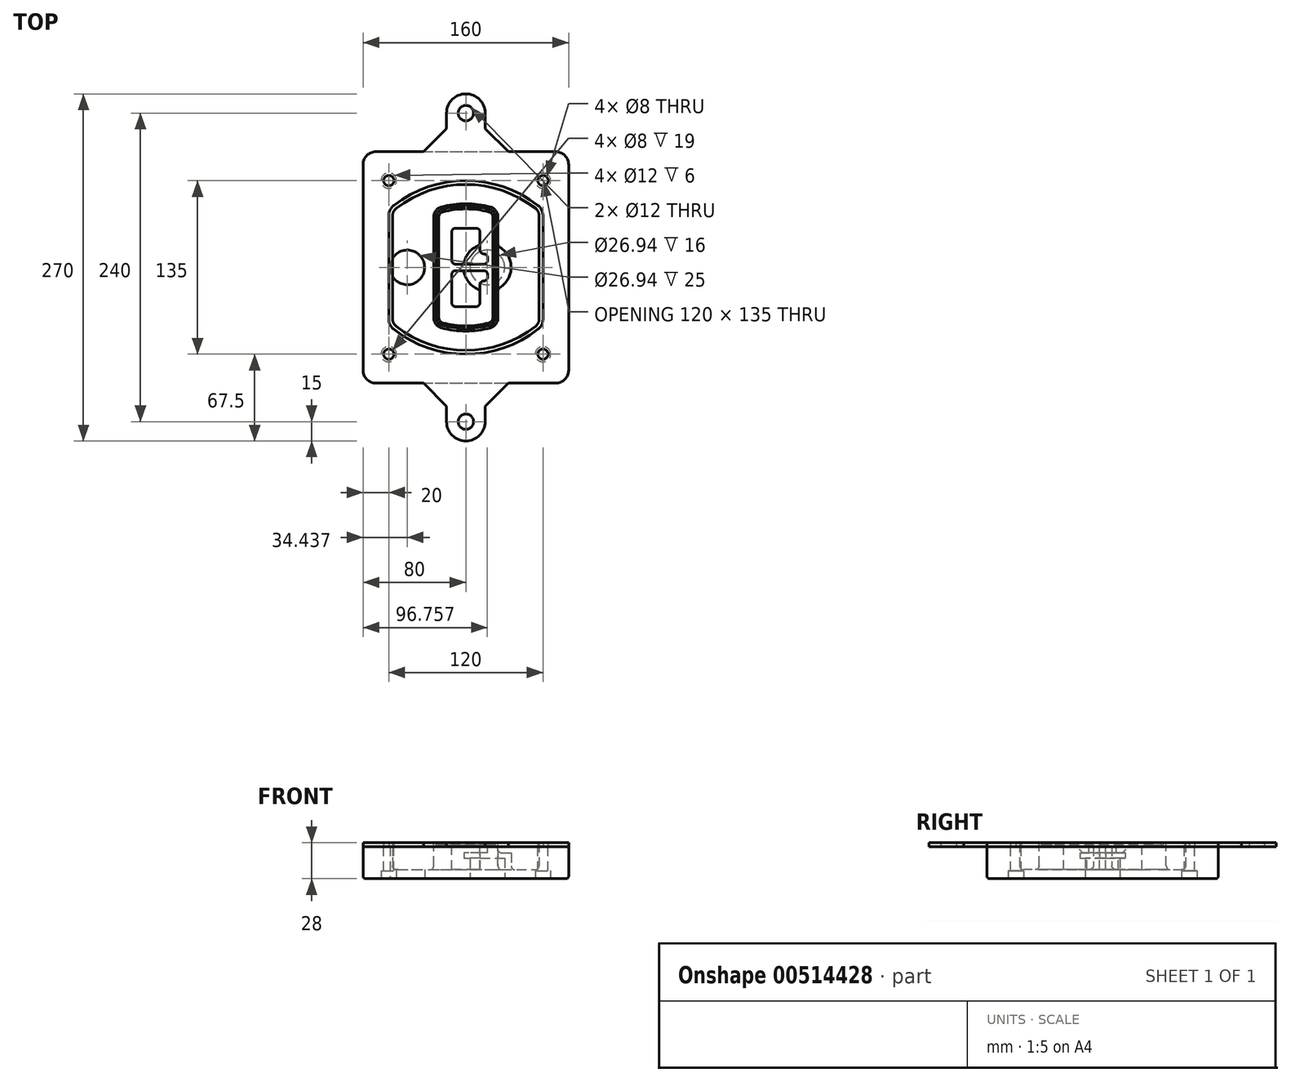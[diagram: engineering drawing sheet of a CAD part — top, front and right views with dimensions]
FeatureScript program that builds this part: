
annotation { "Feature Type Name" : "Feature", "Feature Type Description" : "" }
export const myFeature = defineFeature(function(context is Context, id is Id, definition is map)
    precondition{}
    {
        {
            var Q0;
            Q0=qCreatedBy(makeId("Top.planeOp"),FACE);
            var sketch = newSketch(context, id + "F0", { "sketchPlane" : qUnion([Q0])});
            skPoint(sketch, "E0.rect.middle", {"position": v(0, 0) * mm});
            skLineSegment(sketch, "E1.bottom", {"start": v(-70, -90) * mm, "end": v(70, -90) * mm});
            skLineSegment(sketch, "E1.top", {"start": v(-70, 90) * mm, "end": v(70, 90) * mm});
            skLineSegment(sketch, "E1.left", {"start": v(-80, -80) * mm, "end": v(-80, 80) * mm});
            skLineSegment(sketch, "E1.right", {"start": v(80, -80) * mm, "end": v(80, 80) * mm});
            skLineSegment(sketch, "E2", {"start": v(-80, 90) * mm, "end": v(80, -90) * mm, "construction": true});
            skLineSegment(sketch, "E3", {"start": v(80, 90) * mm, "end": v(-80, -90) * mm, "construction": true});
            skCircle(sketch, "E4", {"center": v(-60, 67.5) * mm, "radius": 4 * mm});
            skCircle(sketch, "E5", {"center": v(60, 67.5) * mm, "radius": 4 * mm});
            skCircle(sketch, "E6", {"center": v(60, -67.5) * mm, "radius": 4 * mm});
            skCircle(sketch, "E7", {"center": v(-60, -67.5) * mm, "radius": 4 * mm});
            skLineSegment(sketch, "E8", {"start": v(-60, 67.5) * mm, "end": v(60, 67.5) * mm, "construction": true});
            skLineSegment(sketch, "E9", {"start": v(60, 67.5) * mm, "end": v(60, -67.5) * mm, "construction": true});
            skLineSegment(sketch, "E10", {"start": v(60, -67.5) * mm, "end": v(-60, -67.5) * mm, "construction": true});
            skLineSegment(sketch, "E11", {"start": v(-60, -67.5) * mm, "end": v(-60, 67.5) * mm, "construction": true});
            skLineSegment(sketch, "E12", {"start": v(-60, 40.3) * mm, "end": v(-60, -40.3) * mm});
            skLineSegment(sketch, "E13", {"start": v(60, 40.3) * mm, "end": v(60, -40.3) * mm});
            skArc(sketch, "E14", {"start": v(56.15, 48.18) * mm, "mid": v(0, 67.5) * mm, "end": v(-56.15, 48.18) * mm});
            skArc(sketch, "E15", {"start": v(-56.15, -48.18) * mm, "mid": v(0, -67.5) * mm, "end": v(56.15, -48.18) * mm});
            skLineSegment(sketch, "E16", {"start": v(-60, 0) * mm, "end": v(60, 0) * mm, "construction": true});
            skPoint(sketch, "E17.visualSharp", {"position": v(-60, -45) * mm});
            skArc(sketch, "E17.filletArc", {"start": v(-60, -40.3) * mm, "mid": v(-58.99, -44.68) * mm, "end": v(-56.15, -48.18) * mm});
            skPoint(sketch, "E18.visualSharp", {"position": v(-60, 45) * mm});
            skArc(sketch, "E18.filletArc", {"start": v(-56.15, 48.18) * mm, "mid": v(-58.99, 44.68) * mm, "end": v(-60, 40.3) * mm});
            skPoint(sketch, "E19.visualSharp", {"position": v(60, 45) * mm});
            skArc(sketch, "E19.filletArc", {"start": v(60, 40.3) * mm, "mid": v(58.99, 44.68) * mm, "end": v(56.15, 48.18) * mm});
            skPoint(sketch, "E20.visualSharp", {"position": v(60, -45) * mm});
            skArc(sketch, "E20.filletArc", {"start": v(56.15, -48.18) * mm, "mid": v(58.99, -44.68) * mm, "end": v(60, -40.3) * mm});
            skPoint(sketch, "E21.visualSharp", {"position": v(-80, 90) * mm});
            skArc(sketch, "E21.filletArc", {"start": v(-70, 90) * mm, "mid": v(-77.07, 87.07) * mm, "end": v(-80, 80) * mm});
            skPoint(sketch, "E22.visualSharp", {"position": v(80, 90) * mm});
            skArc(sketch, "E22.filletArc", {"start": v(80, 80) * mm, "mid": v(77.07, 87.07) * mm, "end": v(70, 90) * mm});
            skPoint(sketch, "E23.visualSharp", {"position": v(80, -90) * mm});
            skArc(sketch, "E23.filletArc", {"start": v(70, -90) * mm, "mid": v(77.07, -87.07) * mm, "end": v(80, -80) * mm});
            skPoint(sketch, "E24.visualSharp", {"position": v(-80, -90) * mm});
            skArc(sketch, "E24.filletArc", {"start": v(-80, -80) * mm, "mid": v(-77.07, -87.07) * mm, "end": v(-70, -90) * mm});
            skArc(sketch, "E25.0", {"start": v(57, 40.3) * mm, "mid": v(56.3, 43.36) * mm, "end": v(54.3, 45.81) * mm});
            skLineSegment(sketch, "E25.1", {"start": v(57, 40.3) * mm, "end": v(57, -40.3) * mm});
            skArc(sketch, "E25.2", {"start": v(54.3, -45.81) * mm, "mid": v(56.3, -43.36) * mm, "end": v(57, -40.3) * mm});
            skArc(sketch, "E25.3", {"start": v(-54.3, -45.81) * mm, "mid": v(0, -64.5) * mm, "end": v(54.3, -45.81) * mm});
            skArc(sketch, "E25.4", {"start": v(-57, -40.3) * mm, "mid": v(-56.3, -43.36) * mm, "end": v(-54.3, -45.81) * mm});
            skArc(sketch, "E25.5", {"start": v(54.3, 45.81) * mm, "mid": v(0, 64.5) * mm, "end": v(-54.3, 45.81) * mm});
            skLineSegment(sketch, "E25.6", {"start": v(-57, 40.3) * mm, "end": v(-57, -40.3) * mm});
            skArc(sketch, "E25.7", {"start": v(-54.3, 45.81) * mm, "mid": v(-56.3, 43.36) * mm, "end": v(-57, 40.3) * mm});
            skArc(sketch, "E26.0", {"start": v(-58.62, 51.33) * mm, "mid": v(-62.58, 46.43) * mm, "end": v(-64, 40.3) * mm});
            skArc(sketch, "E26.1", {"start": v(58.62, 51.33) * mm, "mid": v(0, 71.5) * mm, "end": v(-58.62, 51.33) * mm});
            skArc(sketch, "E26.2", {"start": v(64, 40.3) * mm, "mid": v(62.58, 46.43) * mm, "end": v(58.62, 51.33) * mm});
            skLineSegment(sketch, "E26.3", {"start": v(64, 40.3) * mm, "end": v(64, -40.3) * mm});
            skArc(sketch, "E26.4", {"start": v(58.62, -51.33) * mm, "mid": v(62.58, -46.43) * mm, "end": v(64, -40.3) * mm});
            skLineSegment(sketch, "E26.5", {"start": v(-64, 40.3) * mm, "end": v(-64, -40.3) * mm});
            skArc(sketch, "E26.6", {"start": v(-58.62, -51.33) * mm, "mid": v(0, -71.5) * mm, "end": v(58.62, -51.33) * mm});
            skArc(sketch, "E26.7", {"start": v(-64, -40.3) * mm, "mid": v(-62.58, -46.43) * mm, "end": v(-58.62, -51.33) * mm});
            skSolve(sketch);
        }
        {
            var Q0;
            Q0=makeQuery(id+"F0.imprint","IMPRINT",FACE,{"disambiguationData":[TD([[makeQuery(id+"F0.imprint","IMPRINT",EDGE,{"derivedFrom":sQuery(id+"F0.wireOp",EDGE,"E1.bottom")}),1.0]])]});
            var Q1;
            Q1=makeQuery(id+"F0.imprint","IMPRINT",FACE,{"disambiguationData":[TD([[makeQuery(id+"F0.imprint","IMPRINT",EDGE,{"derivedFrom":sQuery(id+"F0.wireOp",EDGE,"E12")}),1.0]])]});
            var Q2;
            Q2=makeQuery(id+"F0.imprint","IMPRINT",FACE,{"disambiguationData":[TD([[makeQuery(id+"F0.imprint","IMPRINT",EDGE,{"derivedFrom":sQuery(id+"F0.wireOp",EDGE,"E25.0")}),1.0]])]});
            var Q3;
            Q3=makeQuery(id+"F0.imprint","IMPRINT",FACE,{"disambiguationData":[TD([[makeQuery(id+"F0.imprint","IMPRINT",EDGE,{"derivedFrom":sQuery(id+"F0.wireOp",EDGE,"E12")}),-1.0]])]});
            extrude(context, id + "F1", {"entities" : qUnion([Q0, Q1, Q2, Q3]), "oppositeDirection" : true, "depth" : 25 * mm});
        }
        {
            var Q0;
            Q0=makeQuery(id+"F0.imprint","IMPRINT",FACE,{"disambiguationData":[TD([[makeQuery(id+"F0.imprint","IMPRINT",EDGE,{"derivedFrom":sQuery(id+"F0.wireOp",EDGE,"E12")}),1.0]])]});
            extrude(context, id + "F2", {"entities" : qUnion([Q0]), "operationType" : NewBodyOperationType.ADD, "depth" : 3 * mm, "offsetDistance" : 25 * mm});
        }
        {
            var Q0;
            Q0=makeQuery(id+"F0.imprint","IMPRINT",FACE,{"disambiguationData":[TD([[makeQuery(id+"F0.imprint","IMPRINT",EDGE,{"derivedFrom":sQuery(id+"F0.wireOp",EDGE,"E25.0")}),1.0]])]});
            extrude(context, id + "F3", {"entities" : qUnion([Q0]), "operationType" : NewBodyOperationType.REMOVE, "oppositeDirection" : true, "depth" : 18 * mm});
        }
        {
            var Q0;
            Q0=makeQuery(id+"F2.opExtrude","CAP_FACE",FACE,{"disambiguationData":[OSD([sQuery(id+"F0.wireOp",EDGE,"E12"),sQuery(id+"F0.wireOp",EDGE,"E13"),sQuery(id+"F0.wireOp",EDGE,"E14"),sQuery(id+"F0.wireOp",EDGE,"E15"),sQuery(id+"F0.wireOp",EDGE,"E17.filletArc"),sQuery(id+"F0.wireOp",EDGE,"E18.filletArc"),sQuery(id+"F0.wireOp",EDGE,"E19.filletArc"),sQuery(id+"F0.wireOp",EDGE,"E20.filletArc"),sQuery(id+"F0.wireOp",EDGE,"E25.0"),sQuery(id+"F0.wireOp",EDGE,"E25.1"),sQuery(id+"F0.wireOp",EDGE,"E25.2"),sQuery(id+"F0.wireOp",EDGE,"E25.3"),sQuery(id+"F0.wireOp",EDGE,"E25.4"),sQuery(id+"F0.wireOp",EDGE,"E25.5"),sQuery(id+"F0.wireOp",EDGE,"E25.6"),sQuery(id+"F0.wireOp",EDGE,"E25.7")])],"isStart":false});
            var sketch = newSketch(context, id + "F4", { "sketchPlane" : qUnion([Q0])});
            skArc(sketch, "E27.0", {"start": v(-19.08, -46.97) * mm, "mid": v(0, -49.5) * mm, "end": v(19.08, -46.97) * mm});
            skArc(sketch, "E28.0", {"start": v(19.08, 46.97) * mm, "mid": v(0, 49.5) * mm, "end": v(-19.08, 46.97) * mm});
            skLineSegment(sketch, "E29", {"start": v(-25, 39.25) * mm, "end": v(-25, -39.25) * mm});
            skLineSegment(sketch, "E30", {"start": v(25, 39.25) * mm, "end": v(25, -39.25) * mm});
            skLineSegment(sketch, "E31", {"start": v(-25, 45.1) * mm, "end": v(25, 45.1) * mm, "construction": true});
            skLineSegment(sketch, "E32", {"start": v(-25, -45.1) * mm, "end": v(25, -45.1) * mm, "construction": true});
            skPoint(sketch, "E33.visualSharp", {"position": v(-25, 45.1) * mm});
            skArc(sketch, "E33.filletArc", {"start": v(-19.08, 46.97) * mm, "mid": v(-23.35, 44.11) * mm, "end": v(-25, 39.25) * mm});
            skPoint(sketch, "E34.visualSharp", {"position": v(25, 45.1) * mm});
            skArc(sketch, "E34.filletArc", {"start": v(25, 39.25) * mm, "mid": v(23.35, 44.11) * mm, "end": v(19.08, 46.97) * mm});
            skPoint(sketch, "E35.visualSharp", {"position": v(25, -45.1) * mm});
            skArc(sketch, "E35.filletArc", {"start": v(19.08, -46.97) * mm, "mid": v(23.35, -44.11) * mm, "end": v(25, -39.25) * mm});
            skPoint(sketch, "E36.visualSharp", {"position": v(-25, -45.1) * mm});
            skArc(sketch, "E36.filletArc", {"start": v(-25, -39.25) * mm, "mid": v(-23.35, -44.11) * mm, "end": v(-19.08, -46.97) * mm});
            skArc(sketch, "E37.0", {"start": v(54.3, 45.81) * mm, "mid": v(0, 64.5) * mm, "end": v(-54.3, 45.81) * mm});
            skArc(sketch, "E37.1", {"start": v(-54.3, 45.81) * mm, "mid": v(-56.3, 43.36) * mm, "end": v(-57, 40.3) * mm});
            skLineSegment(sketch, "E37.2", {"start": v(-57, 40.3) * mm, "end": v(-57, -40.3) * mm});
            skArc(sketch, "E37.3", {"start": v(-57, -40.3) * mm, "mid": v(-56.3, -43.36) * mm, "end": v(-54.3, -45.81) * mm});
            skArc(sketch, "E37.4", {"start": v(-54.3, -45.81) * mm, "mid": v(0, -64.5) * mm, "end": v(54.3, -45.81) * mm});
            skArc(sketch, "E37.5", {"start": v(54.3, -45.81) * mm, "mid": v(56.3, -43.36) * mm, "end": v(57, -40.3) * mm});
            skLineSegment(sketch, "E37.6", {"start": v(57, 40.3) * mm, "end": v(57, -40.3) * mm});
            skArc(sketch, "E37.7", {"start": v(57, 40.3) * mm, "mid": v(56.3, 43.36) * mm, "end": v(54.3, 45.81) * mm});
            skLineSegment(sketch, "E38.0", {"start": v(23, 39.25) * mm, "end": v(23, -39.25) * mm});
            skArc(sketch, "E38.1", {"start": v(18.56, -45.04) * mm, "mid": v(21.76, -42.9) * mm, "end": v(23, -39.25) * mm});
            skArc(sketch, "E38.2", {"start": v(-18.56, -45.04) * mm, "mid": v(0, -47.5) * mm, "end": v(18.56, -45.04) * mm});
            skArc(sketch, "E38.3", {"start": v(-23, -39.25) * mm, "mid": v(-21.76, -42.9) * mm, "end": v(-18.56, -45.04) * mm});
            skLineSegment(sketch, "E38.4", {"start": v(-23, 39.25) * mm, "end": v(-23, -39.25) * mm});
            skArc(sketch, "E38.5", {"start": v(23, 39.25) * mm, "mid": v(21.76, 42.9) * mm, "end": v(18.56, 45.04) * mm});
            skArc(sketch, "E38.6", {"start": v(-18.56, 45.04) * mm, "mid": v(-21.76, 42.9) * mm, "end": v(-23, 39.25) * mm});
            skArc(sketch, "E38.7", {"start": v(18.56, 45.04) * mm, "mid": v(0, 47.5) * mm, "end": v(-18.56, 45.04) * mm});
            skArc(sketch, "E39.0", {"start": v(21, 39.25) * mm, "mid": v(20.18, 41.68) * mm, "end": v(18.04, 43.1) * mm});
            skLineSegment(sketch, "E39.1", {"start": v(21, 39.25) * mm, "end": v(21, -39.25) * mm});
            skArc(sketch, "E39.2", {"start": v(18.04, -43.1) * mm, "mid": v(20.18, -41.68) * mm, "end": v(21, -39.25) * mm});
            skArc(sketch, "E39.3", {"start": v(-18.04, -43.1) * mm, "mid": v(0, -45.5) * mm, "end": v(18.04, -43.1) * mm});
            skArc(sketch, "E39.4", {"start": v(-21, -39.25) * mm, "mid": v(-20.18, -41.68) * mm, "end": v(-18.04, -43.1) * mm});
            skArc(sketch, "E39.5", {"start": v(18.04, 43.1) * mm, "mid": v(0, 45.5) * mm, "end": v(-18.04, 43.1) * mm});
            skLineSegment(sketch, "E39.6", {"start": v(-21, 39.25) * mm, "end": v(-21, -39.25) * mm});
            skArc(sketch, "E39.7", {"start": v(-18.04, 43.1) * mm, "mid": v(-20.18, 41.68) * mm, "end": v(-21, 39.25) * mm});
            skLineSegment(sketch, "E40", {"start": v(-25, 0) * mm, "end": v(25, 0) * mm, "construction": true});
            skLineSegment(sketch, "E41", {"start": v(-11, 5.5) * mm, "end": v(-11, 27.5) * mm});
            skLineSegment(sketch, "E42", {"start": v(-8, 30.5) * mm, "end": v(8, 30.5) * mm});
            skLineSegment(sketch, "E43", {"start": v(11, 27.5) * mm, "end": v(11, 13.5) * mm});
            skLineSegment(sketch, "E44", {"start": v(14, 10.5) * mm, "end": v(14, 10.5) * mm});
            skLineSegment(sketch, "E45", {"start": v(17, 7.5) * mm, "end": v(17, 5.5) * mm});
            skLineSegment(sketch, "E46", {"start": v(14, 2.5) * mm, "end": v(-8, 2.5) * mm});
            skPoint(sketch, "E47.visualSharp", {"position": v(-11, 30.5) * mm});
            skArc(sketch, "E47.filletArc", {"start": v(-8, 30.5) * mm, "mid": v(-10.12, 29.62) * mm, "end": v(-11, 27.5) * mm});
            skPoint(sketch, "E48.visualSharp", {"position": v(11, 30.5) * mm});
            skArc(sketch, "E48.filletArc", {"start": v(11, 27.5) * mm, "mid": v(10.12, 29.62) * mm, "end": v(8, 30.5) * mm});
            skPoint(sketch, "E49.visualSharp", {"position": v(11, 10.5) * mm});
            skArc(sketch, "E49.filletArc", {"start": v(11, 13.5) * mm, "mid": v(11.88, 11.38) * mm, "end": v(14, 10.5) * mm});
            skPoint(sketch, "E50.visualSharp", {"position": v(17, 10.5) * mm});
            skArc(sketch, "E50.filletArc", {"start": v(17, 7.5) * mm, "mid": v(16.12, 9.62) * mm, "end": v(14, 10.5) * mm});
            skPoint(sketch, "E51.visualSharp", {"position": v(17, 2.5) * mm});
            skArc(sketch, "E51.filletArc", {"start": v(14, 2.5) * mm, "mid": v(16.12, 3.38) * mm, "end": v(17, 5.5) * mm});
            skPoint(sketch, "E52.visualSharp", {"position": v(-11, 2.5) * mm});
            skArc(sketch, "E52.filletArc", {"start": v(-11, 5.5) * mm, "mid": v(-10.12, 3.38) * mm, "end": v(-8, 2.5) * mm});
            skLineSegment(sketch, "E53.0.MirrorCS", {"start": v(14, -2.5) * mm, "end": v(-8, -2.5) * mm});
            skArc(sketch, "E54.0.MirrorCS", {"start": v(-11, -5.5) * mm, "mid": v(-10.12, -3.38) * mm, "end": v(-8, -2.5) * mm});
            skLineSegment(sketch, "E55.0.MirrorCS", {"start": v(-11, -5.5) * mm, "end": v(-11, -27.5) * mm});
            skArc(sketch, "E56.0.MirrorCS", {"start": v(-8, -30.5) * mm, "mid": v(-10.12, -29.62) * mm, "end": v(-11, -27.5) * mm});
            skLineSegment(sketch, "E57.0.MirrorCS", {"start": v(-8, -30.5) * mm, "end": v(8, -30.5) * mm});
            skArc(sketch, "E58.0.MirrorCS", {"start": v(11, -27.5) * mm, "mid": v(10.12, -29.62) * mm, "end": v(8, -30.5) * mm});
            skLineSegment(sketch, "E59.0.MirrorCS", {"start": v(11, -27.5) * mm, "end": v(11, -13.5) * mm});
            skArc(sketch, "E60.0.MirrorCS", {"start": v(11, -13.5) * mm, "mid": v(11.88, -11.38) * mm, "end": v(14, -10.5) * mm});
            skArc(sketch, "E61.0.MirrorCS", {"start": v(17, -7.5) * mm, "mid": v(16.12, -9.62) * mm, "end": v(14, -10.5) * mm});
            skLineSegment(sketch, "E62.0.MirrorCS", {"start": v(17, -7.5) * mm, "end": v(17, -5.5) * mm});
            skArc(sketch, "E63.0.MirrorCS", {"start": v(14, -2.5) * mm, "mid": v(16.12, -3.38) * mm, "end": v(17, -5.5) * mm});
            skSolve(sketch);
        }
        {
            var Q0;
            Q0=makeQuery(id+"F4.imprint","IMPRINT",FACE,{"disambiguationData":[TD([[makeQuery(id+"F4.imprint","IMPRINT",EDGE,{"derivedFrom":sQuery(id+"F4.wireOp",EDGE,"E27.0")}),1.0]])]});
            var Q1;
            Q1=makeQuery(id+"F4.imprint","IMPRINT",FACE,{"disambiguationData":[TD([[makeQuery(id+"F4.imprint","IMPRINT",EDGE,{"derivedFrom":sQuery(id+"F4.wireOp",EDGE,"E38.0")}),-1.0]])]});
            var Q2;
            Q2=makeQuery(id+"F4.imprint","IMPRINT",FACE,{"disambiguationData":[TD([[makeQuery(id+"F4.imprint","IMPRINT",EDGE,{"derivedFrom":sQuery(id+"F4.wireOp",EDGE,"E39.0")}),1.0]])]});
            extrude(context, id + "F5", {"entities" : qUnion([Q0, Q1, Q2]), "operationType" : NewBodyOperationType.ADD, "endBound" : BoundingType.UP_TO_NEXT, "oppositeDirection" : true, "depth" : 25 * mm});
        }
        {
            var Q0;
            Q0=makeQuery(id+"F4.imprint","IMPRINT",FACE,{"disambiguationData":[TD([[makeQuery(id+"F4.imprint","IMPRINT",EDGE,{"derivedFrom":sQuery(id+"F4.wireOp",EDGE,"E38.0")}),-1.0]])]});
            extrude(context, id + "F6", {"entities" : qUnion([Q0]), "operationType" : NewBodyOperationType.REMOVE, "oppositeDirection" : true, "depth" : 2 * mm});
        }
        {
            var Q0;
            Q0=makeQuery(id+"F1.opExtrude","CAP_FACE",FACE,{"disambiguationData":[OSD([sQuery(id+"F0.wireOp",EDGE,"E1.bottom"),sQuery(id+"F0.wireOp",EDGE,"E1.top"),sQuery(id+"F0.wireOp",EDGE,"E1.left"),sQuery(id+"F0.wireOp",EDGE,"E1.right"),sQuery(id+"F0.wireOp",EDGE,"E4"),sQuery(id+"F0.wireOp",EDGE,"E5"),sQuery(id+"F0.wireOp",EDGE,"E6"),sQuery(id+"F0.wireOp",EDGE,"E7"),sQuery(id+"F0.wireOp",EDGE,"E21.filletArc"),sQuery(id+"F0.wireOp",EDGE,"E22.filletArc"),sQuery(id+"F0.wireOp",EDGE,"E23.filletArc"),sQuery(id+"F0.wireOp",EDGE,"E24.filletArc")])],"isStart":false});
            var sketch = newSketch(context, id + "F7", { "sketchPlane" : qUnion([Q0])});
            skCircle(sketch, "E64", {"center": v(16.76, 0) * mm, "radius": 13.47 * mm});
            skCircle(sketch, "E65", {"center": v(-45.56, 0) * mm, "radius": 13.47 * mm});
            skLineSegment(sketch, "E66", {"start": v(80, 0) * mm, "end": v(-80, 0) * mm});
            skCircle(sketch, "E67", {"center": v(16.76, 0) * mm, "radius": 18.47 * mm});
            skCircle(sketch, "E68", {"center": v(60, -67.5) * mm, "radius": 6 * mm});
            skCircle(sketch, "E69", {"center": v(-60, -67.5) * mm, "radius": 6 * mm});
            skCircle(sketch, "E70", {"center": v(-60, 67.5) * mm, "radius": 6 * mm});
            skCircle(sketch, "E71", {"center": v(60, 67.5) * mm, "radius": 6 * mm});
            skSolve(sketch);
        }
        {
            var Q0;
            {var subQ1=sQuery(id+"F7.wireOp",EDGE,"E66");var subQ4=sQuery(id+"F7.wireOp",EDGE,"E64");var subQ6=makeQuery(id+"F7.imprint","INTERSECT",VERTEX,{"disambiguationData":[OD(0.0)],"derivedFrom":[subQ4,subQ1]});Q0=makeQuery(id+"F7.imprint","IMPRINT",FACE,{"disambiguationData":[TD([[makeQuery(id+"F7.imprint","IMPRINT",EDGE,{"disambiguationData":[TD([[subQ6,-1.0]])],"derivedFrom":subQ4}),-1.0]])]});}
            var Q1;
            {var subQ0=sQuery(id+"F7.wireOp",EDGE,"E66");var subQ1=sQuery(id+"F7.wireOp",EDGE,"E64");var subQ3=makeQuery(id+"F7.imprint","INTERSECT",VERTEX,{"disambiguationData":[OD(0.0)],"derivedFrom":[subQ1,subQ0]});Q1=makeQuery(id+"F7.imprint","IMPRINT",FACE,{"disambiguationData":[TD([[makeQuery(id+"F7.imprint","IMPRINT",EDGE,{"disambiguationData":[TD([[subQ3,-1.0]])],"derivedFrom":subQ1}),1.0]])]});}
            var Q2;
            {var subQ0=sQuery(id+"F7.wireOp",EDGE,"E66");var subQ1=sQuery(id+"F7.wireOp",EDGE,"E64");var subQ3=makeQuery(id+"F7.imprint","INTERSECT",VERTEX,{"disambiguationData":[OD(0.0)],"derivedFrom":[subQ1,subQ0]});Q2=makeQuery(id+"F7.imprint","IMPRINT",FACE,{"disambiguationData":[TD([[makeQuery(id+"F7.imprint","IMPRINT",EDGE,{"disambiguationData":[TD([[subQ3,1.0]])],"derivedFrom":subQ1}),1.0]])]});}
            var Q3;
            {var subQ1=sQuery(id+"F7.wireOp",EDGE,"E66");var subQ4=sQuery(id+"F7.wireOp",EDGE,"E64");var subQ6=makeQuery(id+"F7.imprint","INTERSECT",VERTEX,{"disambiguationData":[OD(0.0)],"derivedFrom":[subQ4,subQ1]});Q3=makeQuery(id+"F7.imprint","IMPRINT",FACE,{"disambiguationData":[TD([[makeQuery(id+"F7.imprint","IMPRINT",EDGE,{"disambiguationData":[TD([[subQ6,1.0]])],"derivedFrom":subQ4}),-1.0]])]});}
            extrude(context, id + "F8", {"entities" : qUnion([Q0, Q1, Q2, Q3]), "operationType" : NewBodyOperationType.ADD, "oppositeDirection" : true, "depth" : 20 * mm});
        }
        {
            var Q0;
            {var subQ0=sQuery(id+"F7.wireOp",EDGE,"E66");var subQ1=sQuery(id+"F7.wireOp",EDGE,"E64");var subQ3=makeQuery(id+"F7.imprint","INTERSECT",VERTEX,{"disambiguationData":[OD(0.0)],"derivedFrom":[subQ1,subQ0]});Q0=makeQuery(id+"F7.imprint","IMPRINT",FACE,{"disambiguationData":[TD([[makeQuery(id+"F7.imprint","IMPRINT",EDGE,{"disambiguationData":[TD([[subQ3,-1.0]])],"derivedFrom":subQ1}),1.0]])]});}
            var Q1;
            {var subQ0=sQuery(id+"F7.wireOp",EDGE,"E66");var subQ1=sQuery(id+"F7.wireOp",EDGE,"E64");var subQ3=makeQuery(id+"F7.imprint","INTERSECT",VERTEX,{"disambiguationData":[OD(0.0)],"derivedFrom":[subQ1,subQ0]});Q1=makeQuery(id+"F7.imprint","IMPRINT",FACE,{"disambiguationData":[TD([[makeQuery(id+"F7.imprint","IMPRINT",EDGE,{"disambiguationData":[TD([[subQ3,1.0]])],"derivedFrom":subQ1}),1.0]])]});}
            extrude(context, id + "F9", {"entities" : qUnion([Q0, Q1]), "operationType" : NewBodyOperationType.REMOVE, "oppositeDirection" : true, "depth" : 16 * mm});
        }
        {
            var Q0;
            {var subQ0=sQuery(id+"F7.wireOp",EDGE,"E66");var subQ1=sQuery(id+"F7.wireOp",EDGE,"E65");var subQ3=makeQuery(id+"F7.imprint","INTERSECT",VERTEX,{"disambiguationData":[OD(0.0)],"derivedFrom":[subQ1,subQ0]});Q0=makeQuery(id+"F7.imprint","IMPRINT",FACE,{"disambiguationData":[TD([[makeQuery(id+"F7.imprint","IMPRINT",EDGE,{"disambiguationData":[TD([[subQ3,-1.0]])],"derivedFrom":subQ1}),1.0]])]});}
            var Q1;
            {var subQ0=sQuery(id+"F7.wireOp",EDGE,"E66");var subQ1=sQuery(id+"F7.wireOp",EDGE,"E65");var subQ3=makeQuery(id+"F7.imprint","INTERSECT",VERTEX,{"disambiguationData":[OD(0.0)],"derivedFrom":[subQ1,subQ0]});Q1=makeQuery(id+"F7.imprint","IMPRINT",FACE,{"disambiguationData":[TD([[makeQuery(id+"F7.imprint","IMPRINT",EDGE,{"disambiguationData":[TD([[subQ3,1.0]])],"derivedFrom":subQ1}),1.0]])]});}
            extrude(context, id + "F10", {"entities" : qUnion([Q0, Q1]), "operationType" : NewBodyOperationType.REMOVE, "oppositeDirection" : true, "depth" : 25 * mm});
        }
        {
            var Q0;
            Q0=makeQuery(id+"F7.imprint","IMPRINT",FACE,{"disambiguationData":[TD([[makeQuery(id+"F7.imprint","IMPRINT",EDGE,{"derivedFrom":sQuery(id+"F7.wireOp",EDGE,"E68")}),1.0]])]});
            var Q1;
            Q1=makeQuery(id+"F7.imprint","IMPRINT",FACE,{"disambiguationData":[TD([[makeQuery(id+"F7.imprint","IMPRINT",EDGE,{"derivedFrom":makeQuery(id+"F1.opExtrude","CAP_EDGE",EDGE,{"disambiguationData":[OSD([sQuery(id+"F0.wireOp",EDGE,"E5")])],"isStart":false})}),-1.0]])]});
            var Q2;
            Q2=makeQuery(id+"F7.imprint","IMPRINT",FACE,{"disambiguationData":[TD([[makeQuery(id+"F7.imprint","IMPRINT",EDGE,{"derivedFrom":sQuery(id+"F7.wireOp",EDGE,"E69")}),1.0]])]});
            var Q3;
            Q3=makeQuery(id+"F7.imprint","IMPRINT",FACE,{"disambiguationData":[TD([[makeQuery(id+"F7.imprint","IMPRINT",EDGE,{"derivedFrom":makeQuery(id+"F1.opExtrude","CAP_EDGE",EDGE,{"disambiguationData":[OSD([sQuery(id+"F0.wireOp",EDGE,"E4")])],"isStart":false})}),-1.0]])]});
            var Q4;
            Q4=makeQuery(id+"F7.imprint","IMPRINT",FACE,{"disambiguationData":[TD([[makeQuery(id+"F7.imprint","IMPRINT",EDGE,{"derivedFrom":sQuery(id+"F7.wireOp",EDGE,"E70")}),1.0]])]});
            var Q5;
            Q5=makeQuery(id+"F7.imprint","IMPRINT",FACE,{"disambiguationData":[TD([[makeQuery(id+"F7.imprint","IMPRINT",EDGE,{"derivedFrom":makeQuery(id+"F1.opExtrude","CAP_EDGE",EDGE,{"disambiguationData":[OSD([sQuery(id+"F0.wireOp",EDGE,"E7")])],"isStart":false})}),-1.0]])]});
            var Q6;
            Q6=makeQuery(id+"F7.imprint","IMPRINT",FACE,{"disambiguationData":[TD([[makeQuery(id+"F7.imprint","IMPRINT",EDGE,{"derivedFrom":sQuery(id+"F7.wireOp",EDGE,"E71")}),1.0]])]});
            var Q7;
            Q7=makeQuery(id+"F7.imprint","IMPRINT",FACE,{"disambiguationData":[TD([[makeQuery(id+"F7.imprint","IMPRINT",EDGE,{"derivedFrom":makeQuery(id+"F1.opExtrude","CAP_EDGE",EDGE,{"disambiguationData":[OSD([sQuery(id+"F0.wireOp",EDGE,"E6")])],"isStart":false})}),-1.0]])]});
            extrude(context, id + "F11", {"entities" : qUnion([Q0, Q1, Q2, Q3, Q4, Q5, Q6, Q7]), "operationType" : NewBodyOperationType.REMOVE, "oppositeDirection" : true, "depth" : 6 * mm});
        }
        {
            var Q0;
            Q0=makeQuery(id+"F9.boolean.opBoolean","COPY",FACE,{"derivedFrom":makeQuery(id+"F9.opExtrude","CAP_FACE",FACE,{"disambiguationData":[OSD([sQuery(id+"F7.wireOp",EDGE,"E64")])],"isStart":false})});
            var sketch = newSketch(context, id + "F12", { "sketchPlane" : qUnion([Q0])});
            skArc(sketch, "E72.0", {"start": v(11, 17.55) * mm, "mid": v(2.57, 11.82) * mm, "end": v(-1.54, 2.5) * mm});
            skArc(sketch, "E72.1", {"start": v(-1.54, -2.5) * mm, "mid": v(2.57, -11.82) * mm, "end": v(11, -17.55) * mm});
            skLineSegment(sketch, "E73", {"start": v(-1.54, -2.5) * mm, "end": v(14, -2.5) * mm});
            skLineSegment(sketch, "E74.0", {"start": v(14, 2.5) * mm, "end": v(-1.54, 2.5) * mm});
            skArc(sketch, "E74.1", {"start": v(14, 2.5) * mm, "mid": v(16.12, 3.38) * mm, "end": v(17, 5.5) * mm});
            skLineSegment(sketch, "E74.2", {"start": v(17, 7.5) * mm, "end": v(17, 5.5) * mm});
            skArc(sketch, "E74.3", {"start": v(17, 7.5) * mm, "mid": v(16.12, 9.62) * mm, "end": v(14, 10.5) * mm});
            skArc(sketch, "E74.4", {"start": v(11, 13.5) * mm, "mid": v(11.88, 11.38) * mm, "end": v(14, 10.5) * mm});
            skLineSegment(sketch, "E74.5", {"start": v(11, 17.55) * mm, "end": v(11, 13.5) * mm});
            skLineSegment(sketch, "E74.7", {"start": v(14, -2.5) * mm, "end": v(-1.54, -2.5) * mm});
            skArc(sketch, "E74.8", {"start": v(14, -2.5) * mm, "mid": v(16.12, -3.38) * mm, "end": v(17, -5.5) * mm});
            skLineSegment(sketch, "E74.9", {"start": v(17, -7.5) * mm, "end": v(17, -5.5) * mm});
            skArc(sketch, "E74.10", {"start": v(17, -7.5) * mm, "mid": v(16.12, -9.62) * mm, "end": v(14, -10.5) * mm});
            skArc(sketch, "E74.11", {"start": v(11, -13.5) * mm, "mid": v(11.88, -11.38) * mm, "end": v(14, -10.5) * mm});
            skLineSegment(sketch, "E74.12", {"start": v(11, -17.55) * mm, "end": v(11, -13.5) * mm});
            skPoint(sketch, "E75.orphan", {"position": v(11, -27.5) * mm});
            skPoint(sketch, "E76.orphan", {"position": v(-8, -2.5) * mm});
            skPoint(sketch, "E77.orphan", {"position": v(-8, 2.5) * mm});
            skPoint(sketch, "E78.orphan", {"position": v(11, 27.5) * mm});
            skSolve(sketch);
        }
        {
            var Q0;
            {var subQ7=sQuery(id+"F12.wireOp",EDGE,"E72.0");var subQ14=sQuery(id+"F12.wireOp",EDGE,"E72.1");var subQ16=sQuery(id+"F12.wireOp",EDGE,"E74.1");var subQ18=sQuery(id+"F12.wireOp",EDGE,"E74.8");Q0=qUnion([makeQuery(id+"F12.imprint","IMPRINT",FACE,{"disambiguationData":[TD([[makeQuery(id+"F12.imprint","IMPRINT",EDGE,{"derivedFrom":subQ7}),1.0]])]}),makeQuery(id+"F12.imprint","IMPRINT",FACE,{"disambiguationData":[TD([[makeQuery(id+"F12.imprint","IMPRINT",EDGE,{"derivedFrom":subQ14}),1.0]])]}),makeQuery(id+"F12.imprint","IMPRINT",FACE,{"disambiguationData":[TD([[makeQuery(id+"F12.imprint","IMPRINT",EDGE,{"derivedFrom":subQ16}),1.0]])]}),makeQuery(id+"F12.imprint","IMPRINT",FACE,{"disambiguationData":[TD([[makeQuery(id+"F12.imprint","IMPRINT",EDGE,{"derivedFrom":subQ18}),-1.0]])]})]);}
            var Q1;
            Q1=makeQuery(id+"F5.boolean.opBoolean","SPLIT",FACE,{"disambiguationData":[TD([makeQuery(id+"F5.opExtrude","SWEPT_FACE",FACE,{"disambiguationData":[OSD([sQuery(id+"F4.wireOp",EDGE,"E41")])]})])],"derivedFrom":makeQuery(id+"F3.boolean.opBoolean","COPY",FACE,{"derivedFrom":makeQuery(id+"F3.opExtrude","CAP_FACE",FACE,{"disambiguationData":[OSD([sQuery(id+"F0.wireOp",EDGE,"E25.0"),sQuery(id+"F0.wireOp",EDGE,"E25.1"),sQuery(id+"F0.wireOp",EDGE,"E25.2"),sQuery(id+"F0.wireOp",EDGE,"E25.3"),sQuery(id+"F0.wireOp",EDGE,"E25.4"),sQuery(id+"F0.wireOp",EDGE,"E25.5"),sQuery(id+"F0.wireOp",EDGE,"E25.6"),sQuery(id+"F0.wireOp",EDGE,"E25.7")])],"isStart":false})})});
            extrude(context, id + "F13", {"entities" : qUnion([Q0]), "operationType" : NewBodyOperationType.REMOVE, "endBound" : BoundingType.UP_TO_SURFACE, "endBoundEntityFace" : qUnion([Q1]), "depth" : 25 * mm});
        }
        {
            var Q0;
            Q0=makeQuery(id+"F3.boolean.opBoolean","COPY",EDGE,{"derivedFrom":makeQuery(id+"F3.opExtrude","CAP_EDGE",EDGE,{"disambiguationData":[OSD([sQuery(id+"F0.wireOp",EDGE,"E25.6")])],"isStart":false})});
            var Q1;
            Q1=makeQuery(id+"F8.boolean.opBoolean","INTERSECT",EDGE,{"derivedFrom":[makeQuery(id+"F5.opExtrude","SWEPT_FACE",FACE,{"disambiguationData":[OSD([sQuery(id+"F4.wireOp",EDGE,"E30")])]}),makeQuery(id+"F8.opExtrude","CAP_FACE",FACE,{"disambiguationData":[OSD([sQuery(id+"F7.wireOp",EDGE,"E67")])],"isStart":false})]});
            var Q2;
            Q2=makeQuery(id+"F8.boolean.opBoolean","INTERSECT",EDGE,{"disambiguationData":[OD(1.0)],"derivedFrom":[makeQuery(id+"F5.opExtrude","SWEPT_FACE",FACE,{"disambiguationData":[OSD([sQuery(id+"F4.wireOp",EDGE,"E30")])]}),makeQuery(id+"F8.opExtrude","SWEPT_FACE",FACE,{"disambiguationData":[OSD([sQuery(id+"F7.wireOp",EDGE,"E67")])]})]});
            var Q3;
            {var subQ0=sQuery(id+"F4.wireOp",EDGE,"E30");Q3=makeQuery(id+"F8.boolean.opBoolean","SPLIT",EDGE,{"disambiguationData":[TD([makeQuery(id+"F5.opExtrude","SWEPT_FACE",FACE,{"disambiguationData":[OSD([sQuery(id+"F4.wireOp",EDGE,"E35.filletArc")])]})])],"derivedFrom":makeQuery(id+"F5.opExtrude","CAP_EDGE",EDGE,{"disambiguationData":[OSD([subQ0])],"isStart":false})});}
            var Q4;
            {var subQ0=sQuery(id+"F0.wireOp",EDGE,"E25.7");var subQ1=sQuery(id+"F0.wireOp",EDGE,"E25.1");var subQ2=sQuery(id+"F0.wireOp",EDGE,"E25.6");var subQ3=sQuery(id+"F0.wireOp",EDGE,"E25.5");var subQ4=sQuery(id+"F0.wireOp",EDGE,"E25.4");var subQ5=sQuery(id+"F0.wireOp",EDGE,"E25.0");var subQ6=sQuery(id+"F0.wireOp",EDGE,"E25.2");var subQ7=sQuery(id+"F0.wireOp",EDGE,"E25.3");Q4=makeQuery(id+"F8.boolean.opBoolean","INTERSECT",EDGE,{"derivedFrom":[makeQuery(id+"F5.boolean.opBoolean","SPLIT",FACE,{"disambiguationData":[TD([makeQuery(id+"F2.opExtrude","SWEPT_FACE",FACE,{"disambiguationData":[OSD([subQ5])]})])],"derivedFrom":makeQuery(id+"F3.boolean.opBoolean","COPY",FACE,{"derivedFrom":makeQuery(id+"F3.opExtrude","CAP_FACE",FACE,{"disambiguationData":[OSD([subQ5,subQ1,subQ6,subQ7,subQ4,subQ3,subQ2,subQ0])],"isStart":false})})}),makeQuery(id+"F8.opExtrude","SWEPT_FACE",FACE,{"disambiguationData":[OSD([sQuery(id+"F7.wireOp",EDGE,"E67")])]})]});}
            var Q5;
            Q5=makeQuery(id+"F8.boolean.opBoolean","INTERSECT",EDGE,{"disambiguationData":[OD(0.0)],"derivedFrom":[makeQuery(id+"F5.opExtrude","SWEPT_FACE",FACE,{"disambiguationData":[OSD([sQuery(id+"F4.wireOp",EDGE,"E30")])]}),makeQuery(id+"F8.opExtrude","SWEPT_FACE",FACE,{"disambiguationData":[OSD([sQuery(id+"F7.wireOp",EDGE,"E67")])]})]});
            fillet(context, id + "F14", {"entities" : qUnion([Q0, Q1, Q2, Q3, Q4, Q5]), "radius" : 3 * mm, "tangentPropagation" : true, "allowEdgeOverflow" : false});
        }
        {
            var Q0;
            Q0=makeQuery(id+"F1.opExtrude","CAP_EDGE",EDGE,{"disambiguationData":[OSD([sQuery(id+"F0.wireOp",EDGE,"E1.bottom")])],"isStart":false});
            fillet(context, id + "F15", {"entities" : qUnion([Q0]), "radius" : 2 * mm, "tangentPropagation" : true, "allowEdgeOverflow" : false});
        }
        {
            var Q0;
            {var subQ0=sQuery(id+"F0.wireOp",EDGE,"E21.filletArc");var subQ1=sQuery(id+"F0.wireOp",EDGE,"E7");var subQ2=sQuery(id+"F0.wireOp",EDGE,"E6");var subQ3=sQuery(id+"F0.wireOp",EDGE,"E5");var subQ4=sQuery(id+"F0.wireOp",EDGE,"E4");var subQ5=sQuery(id+"F0.wireOp",EDGE,"E22.filletArc");var subQ6=sQuery(id+"F0.wireOp",EDGE,"E1.bottom");var subQ7=sQuery(id+"F0.wireOp",EDGE,"E1.right");var subQ8=sQuery(id+"F0.wireOp",EDGE,"E1.top");var subQ9=sQuery(id+"F0.wireOp",EDGE,"E1.left");var subQ10=sQuery(id+"F0.wireOp",EDGE,"E23.filletArc");var subQ11=sQuery(id+"F0.wireOp",EDGE,"E24.filletArc");Q0=makeQuery(id+"F2.boolean.opBoolean","SPLIT",FACE,{"disambiguationData":[TD([makeQuery(id+"F1.opExtrude","SWEPT_FACE",FACE,{"disambiguationData":[OSD([subQ6])]})])],"derivedFrom":makeQuery(id+"F1.opExtrude","CAP_FACE",FACE,{"disambiguationData":[OSD([subQ6,subQ8,subQ9,subQ7,subQ4,subQ3,subQ2,subQ1,subQ0,subQ5,subQ10,subQ11])],"isStart":true})});}
            var sketch = newSketch(context, id + "F16", { "sketchPlane" : qUnion([Q0])});
            skLineSegment(sketch, "E79.0", {"start": v(-70, -90) * mm, "end": v(70, -90) * mm});
            skLineSegment(sketch, "E79.1", {"start": v(-60, 40.3) * mm, "end": v(-60, -40.3) * mm});
            skArc(sketch, "E79.2", {"start": v(-56.15, 48.18) * mm, "mid": v(-58.99, 44.68) * mm, "end": v(-60, 40.3) * mm});
            skArc(sketch, "E79.3", {"start": v(56.15, 48.18) * mm, "mid": v(0, 67.5) * mm, "end": v(-56.15, 48.18) * mm});
            skLineSegment(sketch, "E79.4", {"start": v(-70, 90) * mm, "end": v(70, 90) * mm});
            skArc(sketch, "E79.5", {"start": v(-70, 90) * mm, "mid": v(-77.07, 87.07) * mm, "end": v(-80, 80) * mm});
            skCircle(sketch, "E79.6", {"center": v(-60, 67.5) * mm, "radius": 4 * mm});
            skCircle(sketch, "E79.7", {"center": v(60, 67.5) * mm, "radius": 4 * mm});
            skArc(sketch, "E79.8", {"start": v(60, 40.3) * mm, "mid": v(58.99, 44.68) * mm, "end": v(56.15, 48.18) * mm});
            skLineSegment(sketch, "E79.9", {"start": v(60, 40.3) * mm, "end": v(60, -40.3) * mm});
            skArc(sketch, "E79.10", {"start": v(56.15, -48.18) * mm, "mid": v(58.99, -44.68) * mm, "end": v(60, -40.3) * mm});
            skArc(sketch, "E79.11", {"start": v(-56.15, -48.18) * mm, "mid": v(0, -67.5) * mm, "end": v(56.15, -48.18) * mm});
            skLineSegment(sketch, "E79.12", {"start": v(-80, -80) * mm, "end": v(-80, 80) * mm});
            skArc(sketch, "E79.13", {"start": v(-80, -80) * mm, "mid": v(-77.07, -87.07) * mm, "end": v(-70, -90) * mm});
            skCircle(sketch, "E79.14", {"center": v(-60, -67.5) * mm, "radius": 4 * mm});
            skCircle(sketch, "E79.15", {"center": v(60, -67.5) * mm, "radius": 4 * mm});
            skArc(sketch, "E79.16", {"start": v(70, -90) * mm, "mid": v(77.07, -87.07) * mm, "end": v(80, -80) * mm});
            skLineSegment(sketch, "E79.17", {"start": v(80, -80) * mm, "end": v(80, 80) * mm});
            skArc(sketch, "E79.18", {"start": v(80, 80) * mm, "mid": v(77.07, 87.07) * mm, "end": v(70, 90) * mm});
            skArc(sketch, "E79.19", {"start": v(-60, -40.3) * mm, "mid": v(-58.99, -44.68) * mm, "end": v(-56.15, -48.18) * mm});
            skLineSegment(sketch, "E80", {"start": v(15, 108) * mm, "end": v(33, 90) * mm});
            skLineSegment(sketch, "E81", {"start": v(-15, 108) * mm, "end": v(-33, 90) * mm});
            skLineSegment(sketch, "E82", {"start": v(-15, 108) * mm, "end": v(-15, 120) * mm});
            skLineSegment(sketch, "E83", {"start": v(15, 108) * mm, "end": v(15, 120) * mm});
            skArc(sketch, "E84", {"start": v(15, 120) * mm, "mid": v(0, 135) * mm, "end": v(-15, 120) * mm});
            skCircle(sketch, "E85", {"center": v(0, 120) * mm, "radius": 6 * mm});
            skLineSegment(sketch, "E86", {"start": v(-80, 0) * mm, "end": v(80, 0) * mm, "construction": true});
            skLineSegment(sketch, "E87.MirrorCS", {"start": v(-15, -108) * mm, "end": v(-33, -90) * mm});
            skLineSegment(sketch, "E88.MirrorCS", {"start": v(-15, -108) * mm, "end": v(-15, -120) * mm});
            skArc(sketch, "E89.MirrorCS", {"start": v(15, -120) * mm, "mid": v(0, -135) * mm, "end": v(-15, -120) * mm});
            skLineSegment(sketch, "E90.MirrorCS", {"start": v(15, -108) * mm, "end": v(15, -120) * mm});
            skLineSegment(sketch, "E91.MirrorCS", {"start": v(15, -108) * mm, "end": v(33, -90) * mm});
            skCircle(sketch, "E92.MirrorC", {"center": v(0, -120) * mm, "radius": 6 * mm});
            skLineSegment(sketch, "E93", {"start": v(0, 90) * mm, "end": v(0, 120) * mm, "construction": true});
            skSolve(sketch);
        }
        {
            var Q0;
            {var subQ1=sQuery(id+"F16.wireOp",EDGE,"E80");Q0=makeQuery(id+"F16.imprint","IMPRINT",FACE,{"disambiguationData":[TD([[makeQuery(id+"F16.imprint","IMPRINT",EDGE,{"derivedFrom":subQ1}),-1.0]])]});}
            var Q1;
            Q1=makeQuery(id+"F16.imprint","IMPRINT",FACE,{"disambiguationData":[TD([[makeQuery(id+"F16.imprint","IMPRINT",EDGE,{"derivedFrom":sQuery(id+"F16.wireOp",EDGE,"E79.1")}),-1.0]])]});
            var Q2;
            {var subQ0=sQuery(id+"F16.wireOp",EDGE,"E87.MirrorCS");Q2=makeQuery(id+"F16.imprint","IMPRINT",FACE,{"disambiguationData":[TD([[makeQuery(id+"F16.imprint","IMPRINT",EDGE,{"derivedFrom":subQ0}),-1.0]])]});}
            var Q3;
            Q3=makeQuery(id+"F2.opExtrude","CAP_FACE",FACE,{"disambiguationData":[OSD([sQuery(id+"F0.wireOp",EDGE,"E12"),sQuery(id+"F0.wireOp",EDGE,"E13"),sQuery(id+"F0.wireOp",EDGE,"E14"),sQuery(id+"F0.wireOp",EDGE,"E15"),sQuery(id+"F0.wireOp",EDGE,"E17.filletArc"),sQuery(id+"F0.wireOp",EDGE,"E18.filletArc"),sQuery(id+"F0.wireOp",EDGE,"E19.filletArc"),sQuery(id+"F0.wireOp",EDGE,"E20.filletArc"),sQuery(id+"F0.wireOp",EDGE,"E25.0"),sQuery(id+"F0.wireOp",EDGE,"E25.1"),sQuery(id+"F0.wireOp",EDGE,"E25.2"),sQuery(id+"F0.wireOp",EDGE,"E25.3"),sQuery(id+"F0.wireOp",EDGE,"E25.4"),sQuery(id+"F0.wireOp",EDGE,"E25.5"),sQuery(id+"F0.wireOp",EDGE,"E25.6"),sQuery(id+"F0.wireOp",EDGE,"E25.7")])],"isStart":false});
            extrude(context, id + "F17", {"entities" : qUnion([Q0, Q1, Q2]), "endBound" : BoundingType.UP_TO_SURFACE, "depth" : 25 * mm, "endBoundEntityFace" : qUnion([Q3]), "offsetDistance" : 25 * mm});
        }
    });
